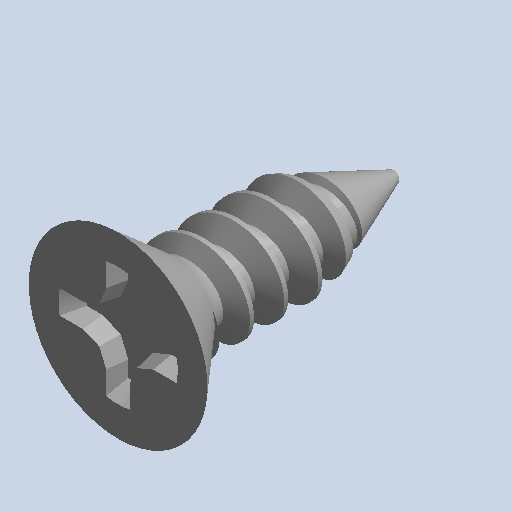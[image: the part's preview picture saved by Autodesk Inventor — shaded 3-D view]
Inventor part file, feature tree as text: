
AUTODESK INVENTOR PART (.ipt)
format: ipt  version: 2022.1 (Build 261234000, 234)  size: 322,048 bytes
history: native  units: mm (DEFAULTED — no unit token found)
features: other x8, revolve x1
bodies: Body1 (feature_tree)
feature tree (9):
  other  "Sólido1"
  other  "Origen"
  other  "Plano YZ"
  other  "Plano XZ"
  other  "Plano XY"
  other  "Eje X"
  other  "Eje Y"
  other  "Eje Z"
  revolve  "Revolve2"  [1 undecoded]
note: 1 required parameter value undecoded (feature->parameter linkage not recoverable at this tier; creation-order binding heuristic only, values carry confidence <= 0.55)
